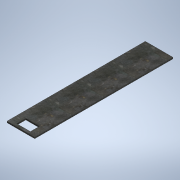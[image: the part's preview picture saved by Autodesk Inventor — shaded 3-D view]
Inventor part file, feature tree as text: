
AUTODESK INVENTOR PART (.ipt)
format: ipt  version: 2020.5 (Build 245400000, 400)  size: 118,784 bytes
history: native  units: mm
features: sketch x3, extrude x2, other x1
ambient origin geometry x8: Origin, YZ Plane, XZ Plane, XY Plane, X Axis, Y Axis, Z Axis, Center Point
bodies: Body1 (feature_tree)
feature tree (6):
  other  "Sólido1"
  sketch  "Boceto1"  dims[d0=152.4mm d1=762.0mm]
  extrude  "Extrusión1"  Depth=762.0mm
  extrude  "Extrusión2"  Depth=14.478mm
  sketch  "Boceto2"  dims[d2=7.62mm d3=0.0mm d4=14.478mm]
  sketch  "Boceto3"  dims[d5=76.2mm d6=50.8mm d7=0.0mm d8=25.4mm d9=0.0mm]
